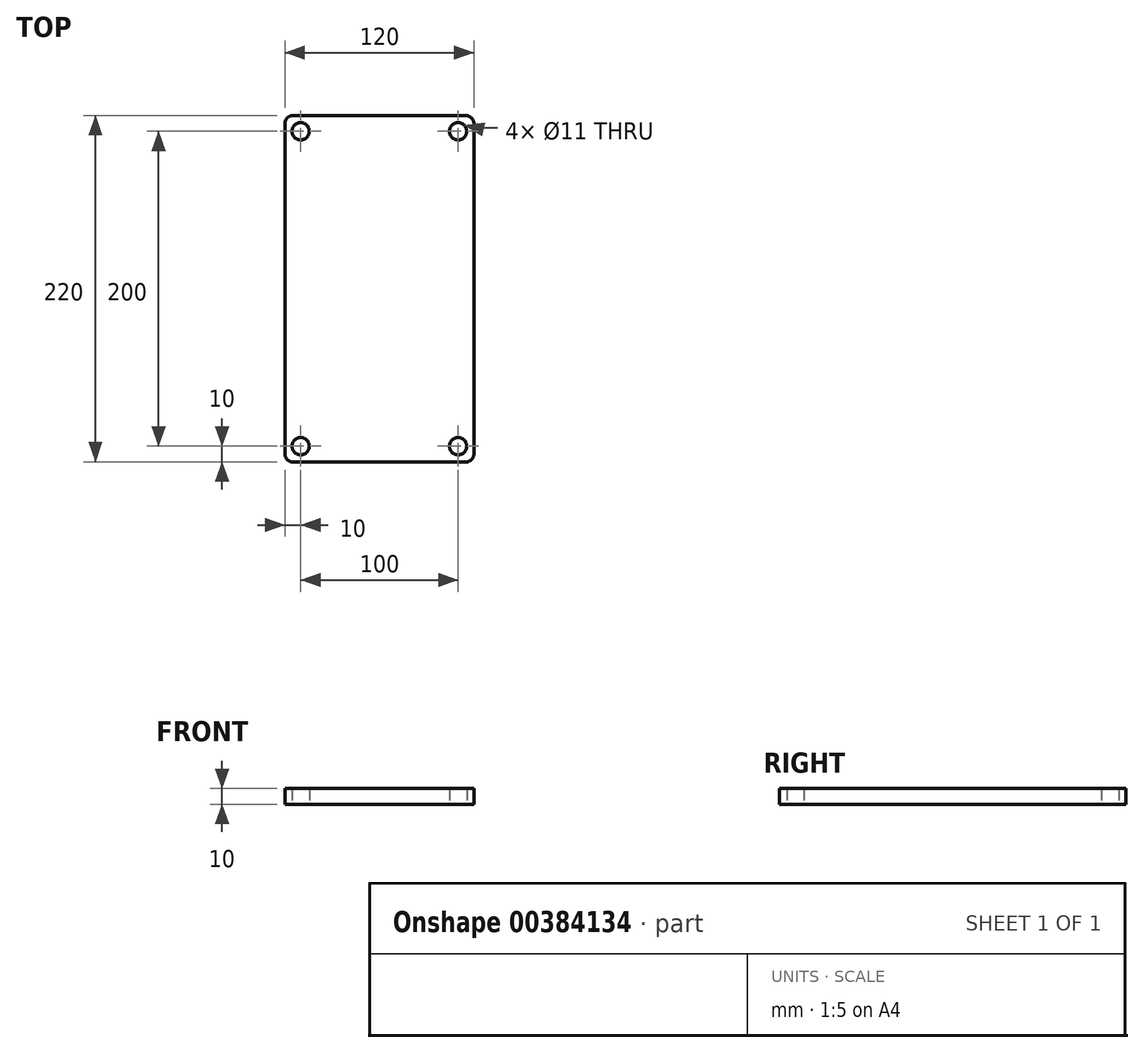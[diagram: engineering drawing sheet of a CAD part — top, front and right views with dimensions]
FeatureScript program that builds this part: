
annotation { "Feature Type Name" : "Feature", "Feature Type Description" : "" }
export const myFeature = defineFeature(function(context is Context, id is Id, definition is map)
    precondition{}
    {
        {
            var Q0;
            Q0=qCreatedBy(makeId("Top.planeOp"),FACE);
            var sketch = newSketch(context, id + "F0", { "sketchPlane" : qUnion([Q0])});
            skLineSegment(sketch, "E0.bottom", {"start": v(55, 110) * mm, "end": v(-55, 110) * mm});
            skLineSegment(sketch, "E0.top", {"start": v(55, -110) * mm, "end": v(-55, -110) * mm});
            skLineSegment(sketch, "E0.left", {"start": v(60, 105) * mm, "end": v(60, -105) * mm});
            skLineSegment(sketch, "E0.right", {"start": v(-60, 105) * mm, "end": v(-60, -105) * mm});
            skPoint(sketch, "E0.middle", {"position": v(0, 0) * mm});
            skPoint(sketch, "E1.visualSharp", {"position": v(60, 110) * mm});
            skArc(sketch, "E1.filletArc", {"start": v(60, 105) * mm, "mid": v(58.54, 108.54) * mm, "end": v(55, 110) * mm});
            skPoint(sketch, "E2.visualSharp", {"position": v(-60, 110) * mm});
            skArc(sketch, "E2.filletArc", {"start": v(-55, 110) * mm, "mid": v(-58.54, 108.54) * mm, "end": v(-60, 105) * mm});
            skPoint(sketch, "E3.visualSharp", {"position": v(-60, -110) * mm});
            skArc(sketch, "E3.filletArc", {"start": v(-60, -105) * mm, "mid": v(-58.54, -108.54) * mm, "end": v(-55, -110) * mm});
            skPoint(sketch, "E4.visualSharp", {"position": v(60, -110) * mm});
            skArc(sketch, "E4.filletArc", {"start": v(55, -110) * mm, "mid": v(58.54, -108.54) * mm, "end": v(60, -105) * mm});
            skCircle(sketch, "E5", {"center": v(-50, 100) * mm, "radius": 5.5 * mm});
            skCircle(sketch, "E6.0.1.0", {"center": v(-50, -100) * mm, "radius": 5.5 * mm});
            skCircle(sketch, "E6.1.0.0", {"center": v(50, 100) * mm, "radius": 5.5 * mm});
            skCircle(sketch, "E6.1.1.0", {"center": v(50, -100) * mm, "radius": 5.5 * mm});
            skLineSegment(sketch, "E6.direction1", {"start": v(-50, 100) * mm, "end": v(50, 100) * mm, "construction": true});
            skLineSegment(sketch, "E6.direction2", {"start": v(-50, 100) * mm, "end": v(-50, -100) * mm, "construction": true});
            skSolve(sketch);
        }
        {
            var Q0;
            Q0=makeQuery(id+"F0.imprint","IMPRINT",FACE,{"disambiguationData":[TD([[makeQuery(id+"F0.imprint","IMPRINT",EDGE,{"derivedFrom":sQuery(id+"F0.wireOp",EDGE,"E0.bottom")}),1.0]])]});
            extrude(context, id + "F1", {"entities" : qUnion([Q0]), "depth" : 10 * mm});
        }
    });
